# Revit family: Lighting-Stradale-GEWISS-STREET[O3]-STAFFA_LUNGA
name_source: partatom
category: Apparecchi per illuminazione
units: mm (PartAtom-declared; Revit-internal decimal feet)

## family parameters
Basato su piano di lavoro = Sì
Condiviso = No
Numero OmniClass = 23.80.00.00
Punto di calcolo locali = No
Quota connettore circolare = Usa diametro
Sempre verticale = Sì
Sorgente d'illuminazione = No
Taglio con vuoti quando caricato = No
Tipo di parte = Normale
Titolo OmniClass = Electric Power and Lighting

## types (1)
- GW87586 - Acciaio zincato - Grigio grafite - 1m
    Altezza da terra testa staffa = 822 mm
    Catalogo = LIGHTING
    Catalogo Serie = STREET [O3]
    Codice EAN = 8011564783058
    Codice Electrocod = 240
    Colore = Grigio grafite
    Descrizione = STREET STAFFA LUNGA 1m GRIGIO GRAFITE
    Descrizione: = Staffa lunga
    IDF = 94cf9e37-c19c-468c-abde-c8e3c61c8187
    IDT = ddb96704-8151-42be-b6b2-ac9eadc1617f
    Immagine tipo = GW87586.jpg
    L_staffa = 120 mm  [stored 0.393701 ft]
    Lunghezza = 1 m
    Materiale = Acciaio zincato
    Modello = GW87586
    Peso (kg) = 6
    Peso (kg): = 6
    Produttore = GEWISS S.p.A.
    Prospetto di default = 1219 mm
    SEO = Staffa
    Scheda Tecnica = https://www.gewiss.com
    Supporti = <Per categoria>
    Tubolare = <Per categoria>
    URL = https://www.gewiss.com
    Versione file RFA = 20.11

note: [stored X ft] marks values corroborated as IEEE doubles in the binary element streams (Revit-internal decimal feet)
